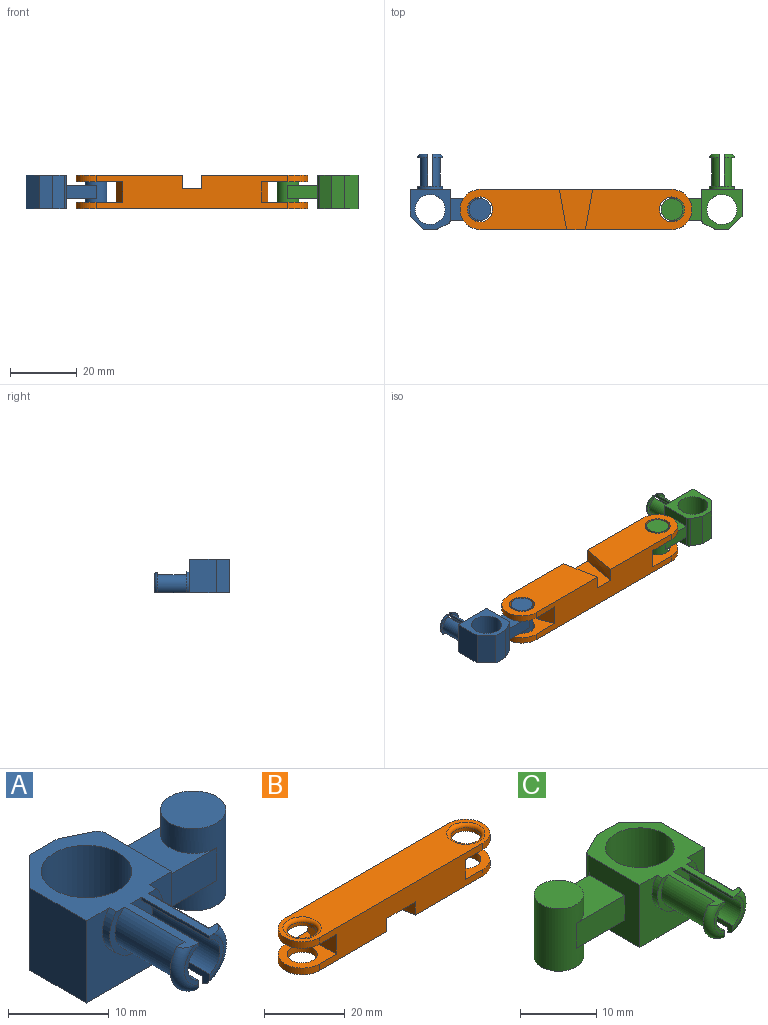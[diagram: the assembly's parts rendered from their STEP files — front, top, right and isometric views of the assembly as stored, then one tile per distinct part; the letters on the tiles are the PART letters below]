
ASSEMBLY  parts=3 mates=2
PART A: 33 faces, bbox 24.4x22.6x11.3 mm
  f0: plane 6.17x3mm, normal (0,1,0), area 5.5mm2, adj f3,f4,f27,f31
  f1: plane 9.5x0.38mm, normal (-1,0,0), area 3.6mm2, adj f2,f4,f5,f6
  f2: cylinder r=2.25mm len=9.5mm, axis (0,1,0), area 52.6mm2, adj f1,f3,f5,f6
  f3: plane 9.64x1.69mm, normal (-1,0,0), area 8mm2, adj f0,f2,f5,f6,f27,f31
  f4: plane 22.5x12mm, normal (0,0,1), area 92.8mm2, adj f0,f1,f5,f6,f7,f8,f10,f11
  f5: plane 5.15x2mm, normal (0,-1,0), area 3.1mm2, adj f1,f2,f3,f4,f31
  f6: plane 7.5x6.25mm, normal (0,-1,0), area 29.7mm2, adj f1,f2,f3,f4,f18,f21,f24,f25
  f7: plane 10x8mm, normal (-1,0,0), area 80mm2, adj f4,f9,f10,f19
  f8: plane 10x9.38mm, normal (1,0,0), area 67.8mm2, adj f4,f9,f14,f15,f16,f17,f19,f20
  f9: plane 12x12mm, normal (0,0,-1), area 68.3mm2, adj f7,f8,f10,f11,f12,f13,f19,f20
  f10: plane 10x4mm, normal (-0.71,0.71,0), area 56.6mm2, adj f4,f7,f9,f13
  f11: plane 10x3.45mm, normal (0.45,0.89,0), area 38.5mm2, adj f4,f9,f13,f20
  f12: cylinder r=4.5mm len=10mm, axis (0,0,-1), area 282.7mm2, adj f4,f9
  f13: plane 10x4mm, normal (0,1,0), area 40mm2, adj f4,f9,f10,f11
  f14: plane 9x4mm, normal (0,1,0), area 36mm2, adj f8,f16,f17,f28
  f15: plane 9x4mm, normal (0,-1,0), area 36mm2, adj f8,f16,f17,f28
  f16: plane 9x6.5mm, normal (0,0,1), area 41.9mm2, adj f8,f14,f15,f28
  f17: plane 9x6.5mm, normal (0,0,-1), area 41.9mm2, adj f8,f14,f15,f28
  f18: cylinder r=3.75mm len=7.5mm, axis (0,-1,0), area 17.3mm2, adj f4,f6,f19
  f19: plane 12x10mm, normal (0,-1,0), area 80.7mm2, adj f4,f7,f8,f9,f18
  f20: cylinder r=1mm len=10mm, axis (0,0,-1), area 11.1mm2, adj f4,f8,f9,f11
  f21: plane 9.64x1.69mm, normal (1,0,0), area 8mm2, adj f6,f22,f23,f24,f26,f32
  f22: plane 5.15x2mm, normal (0,-1,0), area 3.1mm2, adj f4,f21,f24,f25,f32
  f23: plane 6.17x3mm, normal (0,1,0), area 5.5mm2, adj f4,f21,f26,f32
  f24: cylinder r=2.25mm len=9.5mm, axis (0,1,0), area 52.6mm2, adj f6,f21,f22,f25
  f25: plane 9.5x0.38mm, normal (1,0,0), area 3.6mm2, adj f4,f6,f22,f24
  f26: cylinder r=3mm len=8.5mm, axis (0,1,0), area 58.7mm2, adj f4,f6,f21,f23
  f27: cylinder r=3mm len=8.5mm, axis (0,1,0), area 58.7mm2, adj f0,f3,f4,f6
  f28: cylinder r=3.25mm len=10mm, axis (0,0,-1), area 163.4mm2, adj f14,f15,f16,f17,f29,f30
  f29: plane 6.5x6.5mm, normal (0,0,1), area 33.2mm2, adj f28
  f30: plane 6.5x6.5mm, normal (0,0,-1), area 33.2mm2, adj f28
  f31: torus R=2.75mm, axis (0,-1,0), area 11.6mm2, adj f0,f3,f4,f5
  f32: torus R=2.75mm, axis (0,-1,0), area 11.6mm2, adj f4,f21,f22,f23
PART B: 26 faces, bbox 69.5x12.4x10 mm
  f0: plane 57.5x10mm, normal (0,1,0), area 456.5mm2, adj f1,f2,f5,f6,f7,f11,f12,f13
  f1: plane 32.33x12.39mm, normal (0,0,-1), area 309.6mm2, adj f0,f7,f8,f9,f21
  f2: cylinder r=6mm len=12mm, axis (0,0,-1), area 37.7mm2, adj f0,f8,f11,f16
  f3: cylinder r=3.75mm len=7.5mm, axis (0,0,-1), area 23.6mm2, adj f16,f25
  f4: cylinder r=3.75mm len=7.5mm, axis (0,0,-1), area 23.6mm2, adj f13,f24
  f5: cylinder r=6mm len=12mm, axis (0,0,-1), area 37.7mm2, adj f0,f8,f11,f13
  f6: cylinder r=6mm len=12mm, axis (0,0,-1), area 37.7mm2, adj f0,f8,f12,f14
  f7: cylinder r=6mm len=12mm, axis (0,0,-1), area 37.7mm2, adj f0,f1,f8,f17
  f8: plane 57.5x10mm, normal (0,-1,0), area 463mm2, adj f1,f2,f5,f6,f7,f11,f12,f13
  f9: cylinder r=3.75mm len=7.5mm, axis (0,0,-1), area 47.1mm2, adj f1,f17
  f10: cylinder r=3.75mm len=7.5mm, axis (0,0,-1), area 47.1mm2, adj f12,f14
  f11: plane 69.5x12mm, normal (0,0,1), area 661.3mm2, adj f0,f2,f5,f8,f24,f25
  f12: plane 32.33x12.39mm, normal (0,0,-1), area 309.6mm2, adj f0,f6,f8,f10,f22
  f13: plane 14x12mm, normal (0,0,-1), area 89.4mm2, adj f0,f4,f5,f8,f15,f19
  f14: plane 14x12mm, normal (0,0,1), area 89.4mm2, adj f0,f6,f8,f10,f15,f19
  f15: plane 7x6mm, normal (1,0,0), area 42mm2, adj f8,f13,f14,f19
  f16: plane 14x12mm, normal (0,0,-1), area 89.4mm2, adj f0,f2,f3,f8,f18,f20
  f17: plane 14x12mm, normal (0,0,1), area 89.4mm2, adj f0,f7,f8,f9,f18,f20
  f18: plane 7x6mm, normal (-1,0,0), area 42mm2, adj f8,f16,f17,f20
  f19: plane 6x5mm, normal (0.93,0.37,0), area 32.3mm2, adj f0,f13,f14,f15
  f20: plane 6x5mm, normal (-0.93,0.37,0), area 32.3mm2, adj f0,f16,f17,f18
  f21: extruded ~12x4mm, area 48.8mm2, adj f0,f1,f8,f23
  f22: extruded ~12x4mm, area 48.8mm2, adj f0,f8,f12,f23
  f23: plane 12.39x10mm, normal (0,0,-1), area 95.6mm2, adj f0,f8,f21,f22
  f24: torus R=4.75mm, axis (0,0,1), area 40.6mm2, adj f4,f11
  f25: torus R=4.75mm, axis (0,0,1), area 40.6mm2, adj f3,f11
PART C: 33 faces, bbox 24.4x22.6x11.3 mm
  f0: plane 6.17x3mm, normal (0,1,0), area 5.5mm2, adj f3,f4,f27,f31
  f1: plane 9.5x0.38mm, normal (1,0,0), area 3.6mm2, adj f2,f4,f5,f6
  f2: cylinder r=2.25mm len=9.5mm, axis (0,1,0), area 52.6mm2, adj f1,f3,f5,f6
  f3: plane 9.64x1.69mm, normal (1,0,0), area 8mm2, adj f0,f2,f5,f6,f27,f31
  f4: plane 22.5x12mm, normal (0,0,1), area 92.8mm2, adj f0,f1,f5,f6,f7,f8,f10,f11
  f5: plane 5.15x2mm, normal (0,-1,0), area 3.1mm2, adj f1,f2,f3,f4,f31
  f6: plane 7.5x6.25mm, normal (0,-1,0), area 29.7mm2, adj f1,f2,f3,f4,f18,f21,f24,f25
  f7: plane 10x8mm, normal (1,0,0), area 80mm2, adj f4,f9,f10,f19
  f8: plane 10x9.38mm, normal (-1,0,0), area 67.8mm2, adj f4,f9,f14,f15,f16,f17,f19,f20
  f9: plane 12x12mm, normal (0,0,-1), area 68.3mm2, adj f7,f8,f10,f11,f12,f13,f19,f20
  f10: plane 10x4mm, normal (0.71,0.71,0), area 56.6mm2, adj f4,f7,f9,f13
  f11: plane 10x3.45mm, normal (-0.45,0.89,0), area 38.5mm2, adj f4,f9,f13,f20
  f12: cylinder r=4.5mm len=10mm, axis (0,0,-1), area 282.7mm2, adj f4,f9
  f13: plane 10x4mm, normal (0,1,0), area 40mm2, adj f4,f9,f10,f11
  f14: plane 9x4mm, normal (0,1,0), area 36mm2, adj f8,f16,f17,f28
  f15: plane 9x4mm, normal (0,-1,0), area 36mm2, adj f8,f16,f17,f28
  f16: plane 9x6.5mm, normal (0,0,1), area 41.9mm2, adj f8,f14,f15,f28
  f17: plane 9x6.5mm, normal (0,0,-1), area 41.9mm2, adj f8,f14,f15,f28
  f18: cylinder r=3.75mm len=7.5mm, axis (0,-1,0), area 17.3mm2, adj f4,f6,f19
  f19: plane 12x10mm, normal (0,-1,0), area 80.7mm2, adj f4,f7,f8,f9,f18
  f20: cylinder r=1mm len=10mm, axis (0,0,-1), area 11.1mm2, adj f4,f8,f9,f11
  f21: plane 9.64x1.69mm, normal (-1,0,0), area 8mm2, adj f6,f22,f23,f24,f26,f32
  f22: plane 5.15x2mm, normal (0,-1,0), area 3.1mm2, adj f4,f21,f24,f25,f32
  f23: plane 6.17x3mm, normal (0,1,0), area 5.5mm2, adj f4,f21,f26,f32
  f24: cylinder r=2.25mm len=9.5mm, axis (0,1,0), area 52.6mm2, adj f6,f21,f22,f25
  f25: plane 9.5x0.38mm, normal (-1,0,0), area 3.6mm2, adj f4,f6,f22,f24
  f26: cylinder r=3mm len=8.5mm, axis (0,1,0), area 58.7mm2, adj f4,f6,f21,f23
  f27: cylinder r=3mm len=8.5mm, axis (0,1,0), area 58.7mm2, adj f0,f3,f4,f6
  f28: cylinder r=3.25mm len=10mm, axis (0,0,-1), area 163.4mm2, adj f14,f15,f16,f17,f29,f30
  f29: plane 6.5x6.5mm, normal (0,0,1), area 33.2mm2, adj f28
  f30: plane 6.5x6.5mm, normal (0,0,-1), area 33.2mm2, adj f28
  f31: torus R=2.75mm, axis (0,-1,0), area 11.6mm2, adj f0,f3,f4,f5
  f32: torus R=2.75mm, axis (0,-1,0), area 11.6mm2, adj f4,f21,f22,f23
PLACE A rot(axis=(-1,0,0),180deg) t=(-34.56,20.68,112.95)mm
PLACE B rot(axis=(-1,0,0),180deg) t=(50.64,-11.59,112.95)mm
PLACE C rot(axis=(-1,0,0),180deg) t=(94.99,20.68,112.95)mm
MATE fastened C.f28 <-> B.f4  axis (0,0,-1) through (58.96,31.19,102.95)mm
MATE fastened A.f28 <-> B.f2  axis (0,0,-1) through (1.46,31.19,102.95)mm
